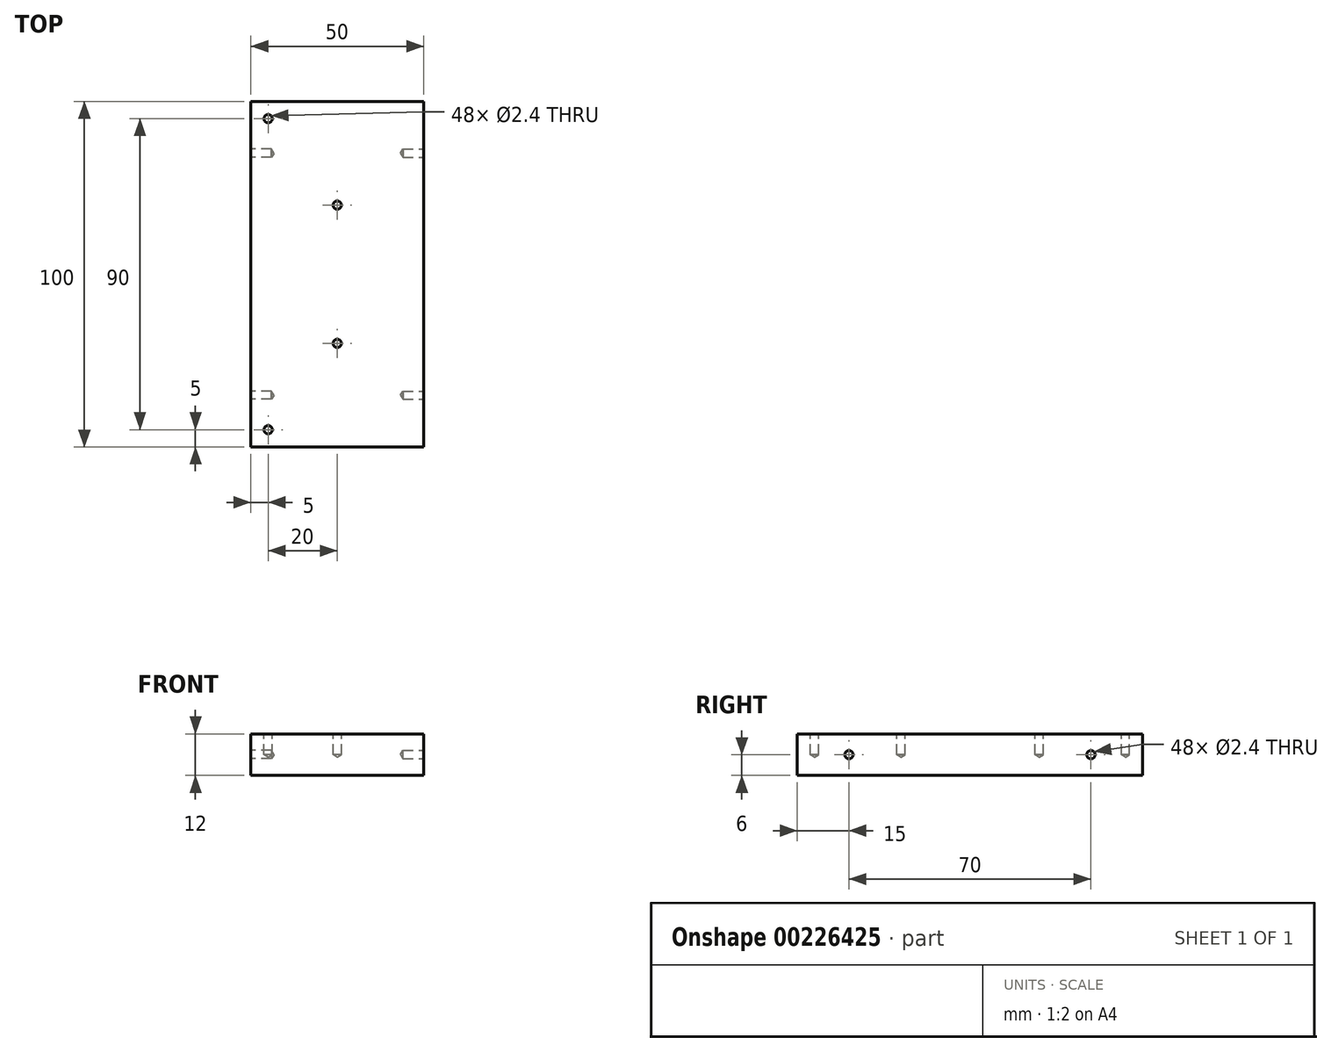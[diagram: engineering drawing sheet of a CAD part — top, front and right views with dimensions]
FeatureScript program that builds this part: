
annotation { "Feature Type Name" : "Feature", "Feature Type Description" : "" }
export const myFeature = defineFeature(function(context is Context, id is Id, definition is map)
    precondition{}
    {
        {
            var Q0;
            Q0=qCreatedBy(makeId("Top.planeOp"),FACE);
            var sketch = newSketch(context, id + "F0", { "sketchPlane" : qUnion([Q0])});
            skLineSegment(sketch, "E0.bottom", {"start": v(25, -50) * mm, "end": v(-25, -50) * mm});
            skLineSegment(sketch, "E0.top", {"start": v(25, 50) * mm, "end": v(-25, 50) * mm});
            skLineSegment(sketch, "E0.left", {"start": v(25, -50) * mm, "end": v(25, 50) * mm});
            skLineSegment(sketch, "E0.right", {"start": v(-25, -50) * mm, "end": v(-25, 50) * mm});
            skPoint(sketch, "E0.middle", {"position": v(0, 0) * mm});
            skSolve(sketch);
        }
        {
            var Q0;
            Q0 = qSketchRegion(id + "F0", true);
            extrude(context, id + "F1", {"entities" : qUnion([Q0]), "depth" : 12 * mm});
        }
        {
            var Q0;
            Q0=makeQuery(id+"F1.opExtrude","CAP_FACE",FACE,{"disambiguationData":[OSD([sQuery(id+"F0.wireOp",EDGE,"E0.bottom"),sQuery(id+"F0.wireOp",EDGE,"E0.top"),sQuery(id+"F0.wireOp",EDGE,"E0.left"),sQuery(id+"F0.wireOp",EDGE,"E0.right")])],"isStart":false});
            var sketch = newSketch(context, id + "F2", { "sketchPlane" : qUnion([Q0])});
            skPoint(sketch, "E1", {"position": v(0, 20) * mm});
            skPoint(sketch, "E2", {"position": v(0, -20) * mm});
            skSolve(sketch);
        }
        {
            var Q0;
            Q0=sQuery(id+"F2.wireOp",VERTEX,"E1");
            var Q1;
            Q1=sQuery(id+"F2.wireOp",VERTEX,"E2");
            var Q2;
            Q2=makeQuery(id+"F1.opExtrude","SWEPT_BODY",BODY,{"disambiguationData":[OSD([sQuery(id+"F0.wireOp",EDGE,"E0.bottom"),sQuery(id+"F0.wireOp",EDGE,"E0.top"),sQuery(id+"F0.wireOp",EDGE,"E0.left"),sQuery(id+"F0.wireOp",EDGE,"E0.right")])]});
            hole(context, id + "F3", {"style" : HoleStyle.SIMPLE, "endStyle" : HoleEndStyle.BLIND, "standardTappedOrClearance" : lookupTablePath({ "standard" : "ISO", "engagement" : "75%", "pitch" : "0.6 mm", "size" : "M3", "type" : "Tapped" }), "standardBlindInLast" : lookupTablePath({ "standard" : "ISO", "engagement" : "75%", "pitch" : "0.6 mm", "size" : "M3", "type" : "Tapped" }), "holeDiameter" : 2.4 * mm, "holeDepth" : 6 * mm, "locations" : qUnion([Q0, Q1]), "scope" : qUnion([Q2])});
        }
        {
            var Q0;
            Q0=makeQuery(id+"F1.opExtrude","SWEPT_FACE",FACE,{"disambiguationData":[OSD([sQuery(id+"F0.wireOp",EDGE,"E0.left")])]});
            var sketch = newSketch(context, id + "F4", { "sketchPlane" : qUnion([Q0])});
            skPoint(sketch, "E3", {"position": v(-35, 6) * mm});
            skPoint(sketch, "E3.positionSnap0", {"position": v(-50, 6) * mm});
            skPoint(sketch, "E4", {"position": v(35, 6) * mm});
            skSolve(sketch);
        }
        {
            var Q0;
            Q0=sQuery(id+"F4.wireOp",VERTEX,"E3");
            var Q1;
            Q1=sQuery(id+"F4.wireOp",VERTEX,"E4");
            var Q2;
            Q2=makeQuery(id+"F1.opExtrude","SWEPT_BODY",BODY,{"disambiguationData":[OSD([sQuery(id+"F0.wireOp",EDGE,"E0.bottom"),sQuery(id+"F0.wireOp",EDGE,"E0.top"),sQuery(id+"F0.wireOp",EDGE,"E0.left"),sQuery(id+"F0.wireOp",EDGE,"E0.right")])]});
            hole(context, id + "F5", {"style" : HoleStyle.SIMPLE, "endStyle" : HoleEndStyle.BLIND, "standardTappedOrClearance" : lookupTablePath({ "standard" : "ISO", "engagement" : "75%", "pitch" : "0.6 mm", "size" : "M3", "type" : "Tapped" }), "standardBlindInLast" : lookupTablePath({ "standard" : "ISO", "engagement" : "75%", "pitch" : "0.6 mm", "size" : "M3", "type" : "Tapped" }), "holeDiameter" : 2.4 * mm, "holeDepth" : 6 * mm, "locations" : qUnion([Q0, Q1]), "scope" : qUnion([Q2])});
        }
        {
            var Q0;
            Q0=makeQuery(id+"F1.opExtrude","SWEPT_FACE",FACE,{"disambiguationData":[OSD([sQuery(id+"F0.wireOp",EDGE,"E0.right")])]});
            var sketch = newSketch(context, id + "F6", { "sketchPlane" : qUnion([Q0])});
            skPoint(sketch, "E5.positionSnap0", {"position": v(-50, 6) * mm});
            skPoint(sketch, "E6", {"position": v(-35, 6) * mm});
            skPoint(sketch, "E7", {"position": v(35, 6) * mm});
            skSolve(sketch);
        }
        {
            var Q0;
            Q0=sQuery(id+"F6.wireOp",VERTEX,"E6");
            var Q1;
            Q1=sQuery(id+"F6.wireOp",VERTEX,"E7");
            var Q2;
            Q2=makeQuery(id+"F1.opExtrude","SWEPT_BODY",BODY,{"disambiguationData":[OSD([sQuery(id+"F0.wireOp",EDGE,"E0.bottom"),sQuery(id+"F0.wireOp",EDGE,"E0.top"),sQuery(id+"F0.wireOp",EDGE,"E0.left"),sQuery(id+"F0.wireOp",EDGE,"E0.right")])]});
            hole(context, id + "F7", {"style" : HoleStyle.SIMPLE, "endStyle" : HoleEndStyle.BLIND, "standardTappedOrClearance" : lookupTablePath({ "standard" : "ISO", "engagement" : "75%", "pitch" : "0.6 mm", "size" : "M3", "type" : "Tapped" }), "standardBlindInLast" : lookupTablePath({ "standard" : "ISO", "engagement" : "75%", "pitch" : "0.6 mm", "size" : "M3", "type" : "Tapped" }), "holeDiameter" : 2.4 * mm, "holeDepth" : 6 * mm, "locations" : qUnion([Q0, Q1]), "scope" : qUnion([Q2])});
        }
        {
            var Q0;
            Q0=makeQuery(id+"F2.imprint","IMPRINT",FACE,{"disambiguationData":[TD([[makeQuery(id+"F2.imprint","IMPRINT",EDGE,{"derivedFrom":makeQuery(id+"F1.opExtrude","CAP_EDGE",EDGE,{"disambiguationData":[OSD([sQuery(id+"F0.wireOp",EDGE,"E0.bottom")])],"isStart":false})}),-1.0]])]});
            var sketch = newSketch(context, id + "F8", { "sketchPlane" : qUnion([Q0])});
            skPoint(sketch, "E8", {"position": v(-20, 45) * mm});
            skPoint(sketch, "E9", {"position": v(-20, -45) * mm});
            skSolve(sketch);
        }
        {
            var Q0;
            Q0=sQuery(id+"F8.wireOp",VERTEX,"E9");
            var Q1;
            Q1=sQuery(id+"F8.wireOp",VERTEX,"E8");
            var Q2;
            Q2=makeQuery(id+"F1.opExtrude","SWEPT_BODY",BODY,{"disambiguationData":[OSD([sQuery(id+"F0.wireOp",EDGE,"E0.bottom"),sQuery(id+"F0.wireOp",EDGE,"E0.top"),sQuery(id+"F0.wireOp",EDGE,"E0.left"),sQuery(id+"F0.wireOp",EDGE,"E0.right")])]});
            hole(context, id + "F9", {"style" : HoleStyle.SIMPLE, "endStyle" : HoleEndStyle.BLIND, "standardTappedOrClearance" : lookupTablePath({ "standard" : "ISO", "engagement" : "75%", "pitch" : "0.6 mm", "size" : "M3", "type" : "Tapped" }), "standardBlindInLast" : lookupTablePath({ "standard" : "ISO", "engagement" : "75%", "pitch" : "0.6 mm", "size" : "M3", "type" : "Tapped" }), "holeDiameter" : 2.4 * mm, "holeDepth" : 6 * mm, "locations" : qUnion([Q0, Q1]), "scope" : qUnion([Q2])});
        }
    });
